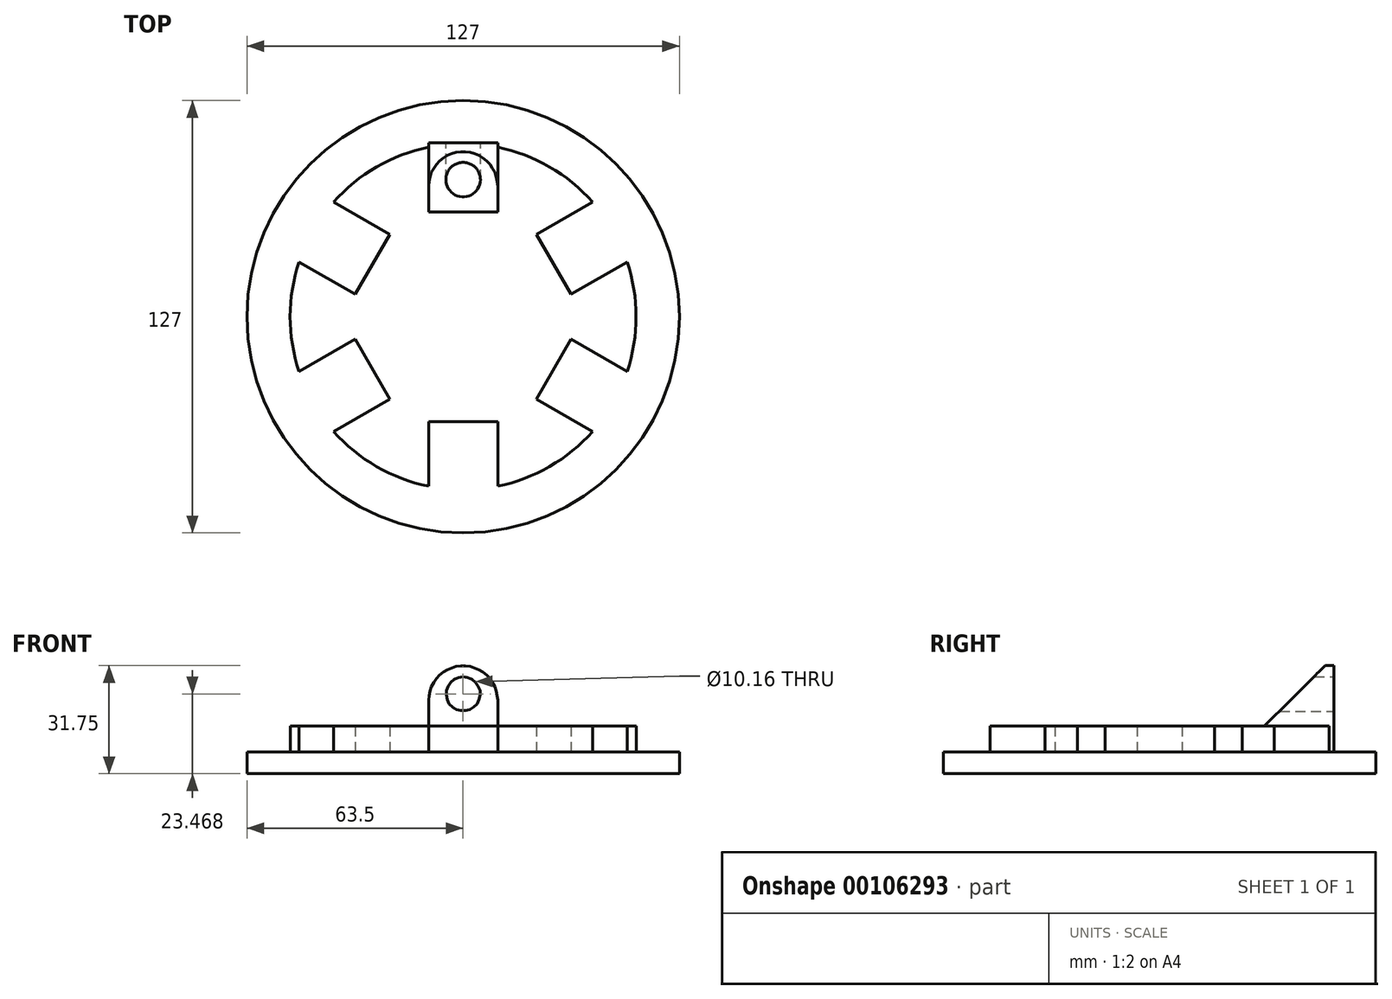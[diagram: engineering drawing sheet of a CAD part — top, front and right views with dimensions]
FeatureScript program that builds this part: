
annotation { "Feature Type Name" : "Feature", "Feature Type Description" : "" }
export const myFeature = defineFeature(function(context is Context, id is Id, definition is map)
    precondition{}
    {
        {
            var Q0;
            Q0=qCreatedBy(makeId("Top.planeOp"),FACE);
            var sketch = newSketch(context, id + "F0", { "sketchPlane" : qUnion([Q0])});
            skCircle(sketch, "E0", {"center": v(0, 0) * mm, "radius": 63.5 * mm});
            skSolve(sketch);
        }
        {
            var Q0;
            Q0=makeQuery(id+"F0.imprint","IMPRINT",FACE,{"disambiguationData":[TD([[makeQuery(id+"F0.imprint","IMPRINT",EDGE,{"derivedFrom":sQuery(id+"F0.wireOp",EDGE,"E0")}),1.0]])]});
            extrude(context, id + "F1", {"entities" : qUnion([Q0]), "depth" : 6.35 * mm});
        }
        {
            var Q0;
            Q0=makeQuery(id+"F1.opExtrude","CAP_FACE",FACE,{"disambiguationData":[OSD([sQuery(id+"F0.wireOp",EDGE,"E0")])],"isStart":false});
            var sketch = newSketch(context, id + "F2", { "sketchPlane" : qUnion([Q0])});
            skLineSegment(sketch, "E1.bottom", {"start": v(-10.16, 51.1) * mm, "end": v(10.16, 51.1) * mm});
            skLineSegment(sketch, "E1.top", {"start": v(-10.16, 30.77) * mm, "end": v(10.16, 30.77) * mm});
            skLineSegment(sketch, "E1.left", {"start": v(-10.16, 51.1) * mm, "end": v(-10.16, 30.77) * mm});
            skLineSegment(sketch, "E1.right", {"start": v(10.16, 51.1) * mm, "end": v(10.16, 30.77) * mm});
            skSolve(sketch);
        }
        {
            var Q0;
            Q0=makeQuery(id+"F2.imprint","IMPRINT",FACE,{"disambiguationData":[TD([[makeQuery(id+"F2.imprint","IMPRINT",EDGE,{"derivedFrom":sQuery(id+"F2.wireOp",EDGE,"E1.bottom")}),-1.0]])]});
            extrude(context, id + "F3", {"entities" : qUnion([Q0]), "operationType" : NewBodyOperationType.ADD, "depth" : 25.4 * mm});
        }
        {
            var Q0;
            Q0=makeQuery(id+"F3.opExtrude","SWEPT_FACE",FACE,{"disambiguationData":[OSD([sQuery(id+"F2.wireOp",EDGE,"E1.bottom")])]});
            var sketch = newSketch(context, id + "F4", { "sketchPlane" : qUnion([Q0])});
            skPoint(sketch, "E2", {"position": v(0, 23.47) * mm});
            skSolve(sketch);
        }
        {
            var Q0;
            Q0=sQuery(id+"F4.wireOp",VERTEX,"E2");
            var Q1;
            Q1=makeQuery(id+"F1.opExtrude","SWEPT_BODY",BODY,{"disambiguationData":[OSD([sQuery(id+"F0.wireOp",EDGE,"E0")])]});
            hole(context, id + "F5", {"style" : HoleStyle.SIMPLE, "endStyle" : HoleEndStyle.THROUGH, "holeDiameter" : 10.16 * mm, "startFromSketch" : true, "locations" : qUnion([Q0]), "scope" : qUnion([Q1]), "isTappedThrough" : true});
        }
        {
            var Q0;
            Q0=makeQuery(id+"F3.opExtrude","CAP_EDGE",EDGE,{"disambiguationData":[OSD([sQuery(id+"F2.wireOp",EDGE,"E1.top")])],"isStart":false});
            chamfer(context, id + "F6", {"entities" : qUnion([Q0]), "chamferType" : ChamferType.TWO_OFFSETS, "width1" : 17.78 * mm, "oppositeDirection" : false, "width2" : 17.78 * mm, "tangentPropagation" : true});
        }
        {
            var Q0;
            Q0=makeQuery(id+"F3.opExtrude","CAP_EDGE",EDGE,{"disambiguationData":[OSD([sQuery(id+"F2.wireOp",EDGE,"E1.right")])],"isStart":false});
            var Q1;
            Q1=makeQuery(id+"F3.opExtrude","CAP_EDGE",EDGE,{"disambiguationData":[OSD([sQuery(id+"F2.wireOp",EDGE,"E1.left")])],"isStart":false});
            fillet(context, id + "F7", {"entities" : qUnion([Q0, Q1]), "radius" : 10.16 * mm, "tangentPropagation" : true, "allowEdgeOverflow" : false});
        }
        {
            var Q0;
            Q0=qCreatedBy(makeId("Front.planeOp"),FACE);
            var sketch = newSketch(context, id + "F8", { "sketchPlane" : qUnion([Q0])});
            skLineSegment(sketch, "E3", {"start": v(0, 62.55) * mm, "end": v(0, 47.48) * mm});
            skSolve(sketch);
        }
        {
            var Q0;
            Q0=makeQuery(id+"F1.opExtrude","CAP_FACE",FACE,{"disambiguationData":[OSD([sQuery(id+"F0.wireOp",EDGE,"E0")])],"isStart":false});
            var sketch = newSketch(context, id + "F9", { "sketchPlane" : qUnion([Q0])});
            skArc(sketch, "E4", {"start": v(-10.16, 49.77) * mm, "mid": v(-25.4, 44) * mm, "end": v(-38.03, 33.69) * mm});
            skLineSegment(sketch, "E5", {"start": v(-10.16, 49.77) * mm, "end": v(-10.16, 30.77) * mm});
            skLineSegment(sketch, "E6", {"start": v(-10.16, 30.77) * mm, "end": v(10.16, 30.77) * mm});
            skLineSegment(sketch, "E7", {"start": v(10.16, 30.77) * mm, "end": v(10.16, 49.77) * mm});
            skLineSegment(sketch, "E8", {"start": v(38.03, 33.69) * mm, "end": v(21.57, 24.19) * mm});
            skLineSegment(sketch, "E9", {"start": v(21.57, 24.19) * mm, "end": v(31.73, 6.59) * mm});
            skLineSegment(sketch, "E10", {"start": v(31.73, 6.59) * mm, "end": v(48.19, 16.09) * mm});
            skLineSegment(sketch, "E11", {"start": v(48.19, -16.09) * mm, "end": v(31.73, -6.59) * mm});
            skLineSegment(sketch, "E12", {"start": v(31.73, -6.59) * mm, "end": v(21.57, -24.19) * mm});
            skLineSegment(sketch, "E13", {"start": v(21.57, -24.19) * mm, "end": v(38.03, -33.69) * mm});
            skLineSegment(sketch, "E14", {"start": v(10.16, -49.77) * mm, "end": v(10.16, -30.77) * mm});
            skLineSegment(sketch, "E15", {"start": v(10.16, -30.77) * mm, "end": v(-10.16, -30.77) * mm});
            skLineSegment(sketch, "E16", {"start": v(-10.16, -30.77) * mm, "end": v(-10.16, -49.77) * mm});
            skLineSegment(sketch, "E17", {"start": v(-38.03, -33.69) * mm, "end": v(-21.57, -24.19) * mm});
            skLineSegment(sketch, "E18", {"start": v(-21.57, -24.19) * mm, "end": v(-31.73, -6.59) * mm});
            skLineSegment(sketch, "E19", {"start": v(-31.73, -6.59) * mm, "end": v(-48.19, -16.09) * mm});
            skLineSegment(sketch, "E20", {"start": v(-38.03, 33.69) * mm, "end": v(-21.57, 24.19) * mm});
            skLineSegment(sketch, "E21", {"start": v(-21.57, 24.19) * mm, "end": v(-31.73, 6.59) * mm});
            skLineSegment(sketch, "E22", {"start": v(-31.73, 6.59) * mm, "end": v(-48.19, 16.09) * mm});
            skArc(sketch, "E23.trimOffspring", {"start": v(-48.19, 16.09) * mm, "mid": v(-50.8, 0) * mm, "end": v(-48.19, -16.09) * mm});
            skArc(sketch, "E24.trimOffspring", {"start": v(-38.03, -33.69) * mm, "mid": v(-25.4, -44) * mm, "end": v(-10.16, -49.77) * mm});
            skArc(sketch, "E25.trimOffspring", {"start": v(38.03, 33.69) * mm, "mid": v(25.4, 44) * mm, "end": v(10.16, 49.77) * mm});
            skArc(sketch, "E26.trimOffspring", {"start": v(48.19, -16.09) * mm, "mid": v(50.8, 0) * mm, "end": v(48.19, 16.09) * mm});
            skArc(sketch, "E27.trimOffspring", {"start": v(10.16, -49.77) * mm, "mid": v(25.4, -44) * mm, "end": v(38.03, -33.69) * mm});
            skSolve(sketch);
        }
        {
            var Q0;
            Q0=makeQuery(id+"F9.imprint","IMPRINT",FACE,{"disambiguationData":[TD([[makeQuery(id+"F9.imprint","IMPRINT",EDGE,{"derivedFrom":sQuery(id+"F9.wireOp",EDGE,"E4")}),1.0]])]});
            extrude(context, id + "F10", {"entities" : qUnion([Q0]), "operationType" : NewBodyOperationType.ADD, "depth" : 7.62 * mm});
        }
    });
